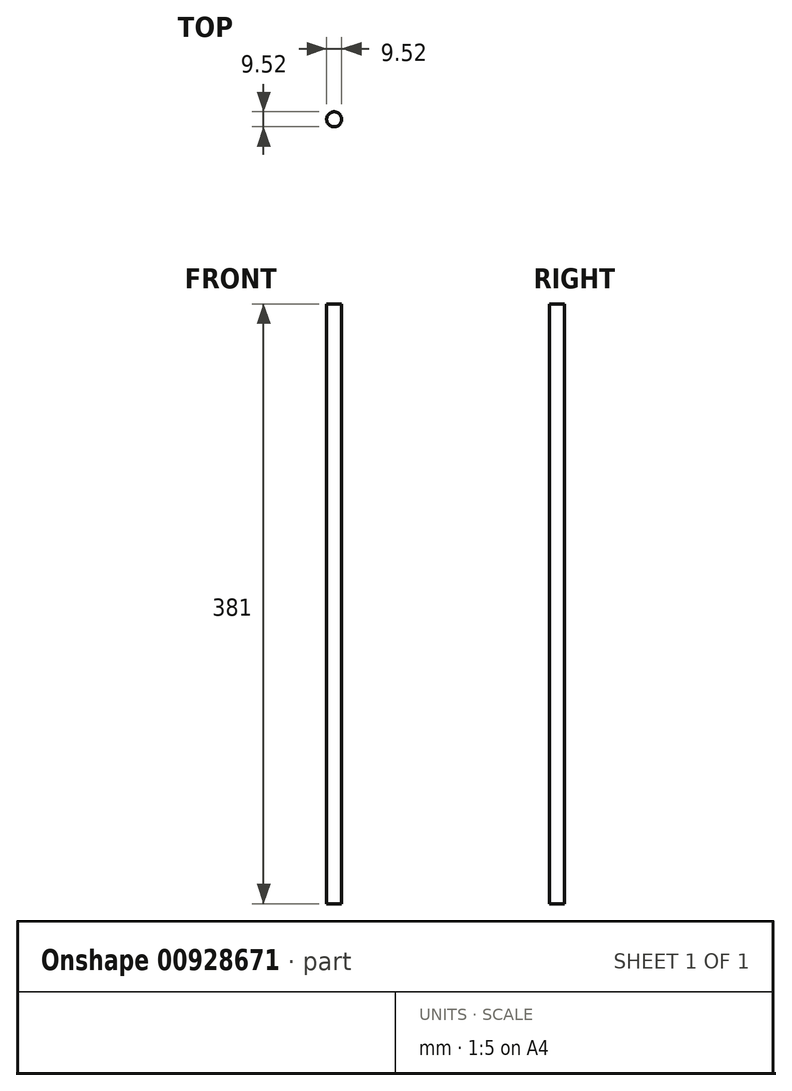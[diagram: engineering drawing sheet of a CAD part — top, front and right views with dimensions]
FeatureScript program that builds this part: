
annotation { "Feature Type Name" : "Feature", "Feature Type Description" : "" }
export const myFeature = defineFeature(function(context is Context, id is Id, definition is map)
    precondition{}
    {
        {
            var Q0;
            Q0=qCreatedBy(makeId("Top.planeOp"),FACE);
            var sketch = newSketch(context, id + "F0", { "sketchPlane" : qUnion([Q0])});
            skCircle(sketch, "E0", {"center": v(0, 0) * mm, "radius": 4.76 * mm});
            skSolve(sketch);
        }
        {
            var Q0;
            Q0 = qSketchRegion(id + "F0", true);
            extrude(context, id + "F1", {"entities" : qUnion([Q0]), "depth" : 381 * mm, "offsetDistance" : 25.4 * mm});
        }
    });
